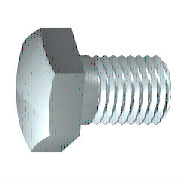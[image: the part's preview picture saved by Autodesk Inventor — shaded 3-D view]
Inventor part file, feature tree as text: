
AUTODESK INVENTOR PART (.ipt)
format: ipt  version: 2023.2 (Build 272271030, 271C)  size: 189,440 bytes
history: native  units: mm (DEFAULTED — no unit token found)
features: sketch x3, extrude x1, chamfer x1, plane x1
ambient origin geometry x7: Origin, YZ Plane, XZ Plane, X Axis, Y Axis, Z Axis, Center Point
bodies: Solid1 (feature_tree), Body (feature_tree)
feature tree (6):
  extrude  "Head"  Depth=114.0mm
  chamfer  "Chamfer1"  Distance=8.2mm
  plane  "Work Plane1"
  sketch  "Sketch1"  dims[d0=120.0mm d1=114.0mm]
  sketch  "Sketch2"  dims[d2=14.0mm]
  sketch  "Sketch4"  dims[d12=90.0deg d3=8.2mm d4=0.0mm d5=30.0deg d21=90.0deg d6=1.2269mm d7=1.227mm d8=0.0mm d9=0.6001mm d10=19.64mm d11=21.0mm d13=1.227mm d14=14.0mm d15=114.0mm d16=0.0mm d19=21.0mm d55=45.0deg d57=0.0mm d58=0.0mm]
